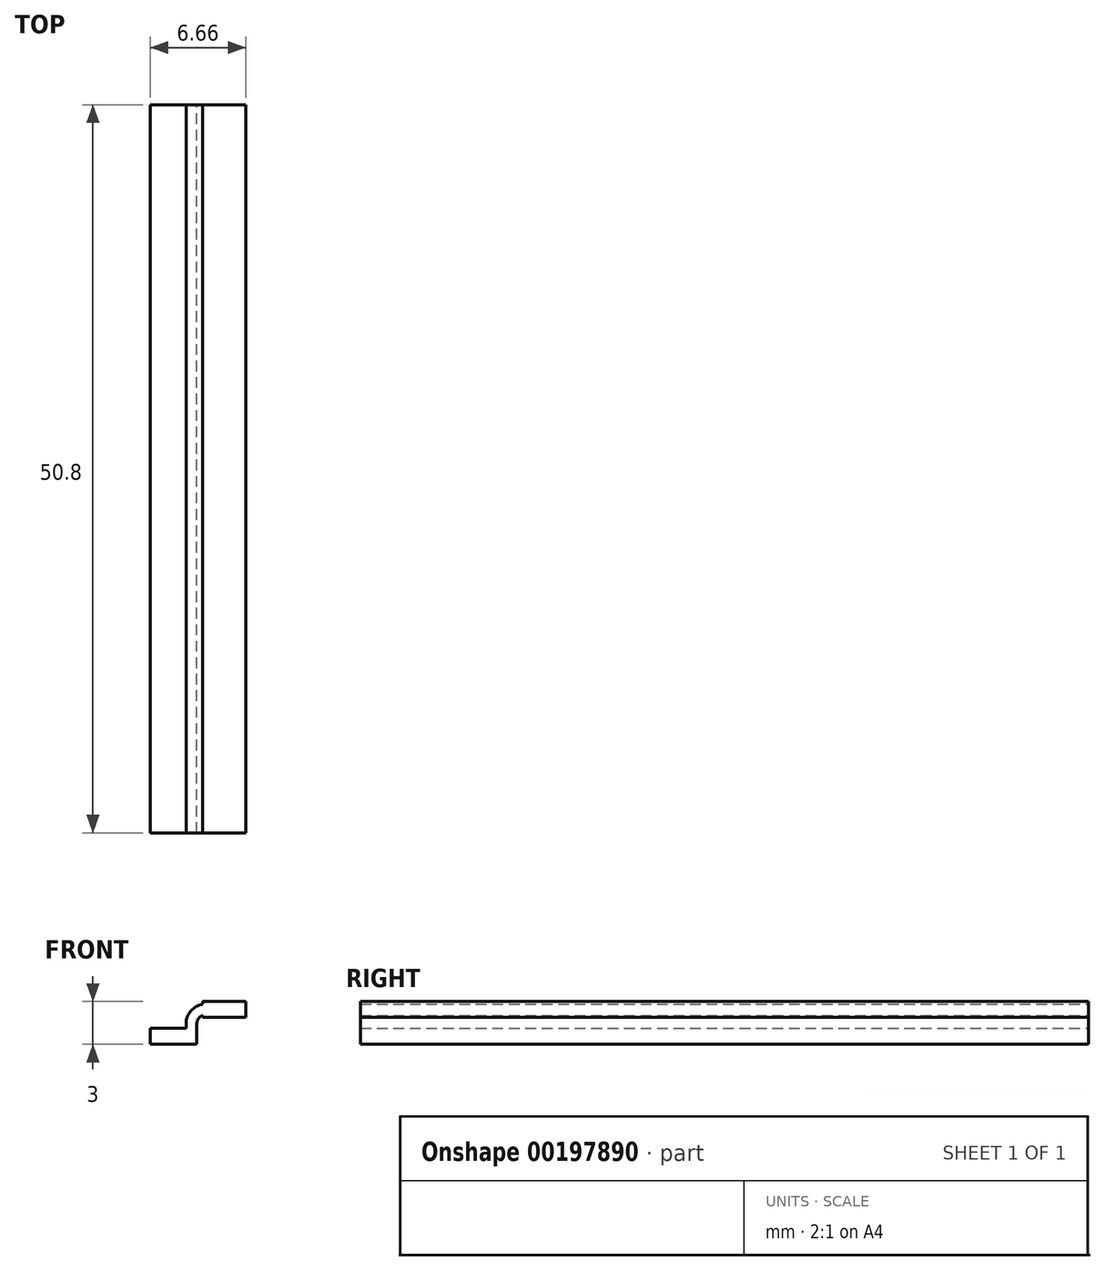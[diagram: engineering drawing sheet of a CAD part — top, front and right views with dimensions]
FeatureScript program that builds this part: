
annotation { "Feature Type Name" : "Feature", "Feature Type Description" : "" }
export const myFeature = defineFeature(function(context is Context, id is Id, definition is map)
    precondition{}
    {
        {
            var Q0;
            Q0=qCreatedBy(makeId("Front.planeOp"),FACE);
            var sketch = newSketch(context, id + "F0", { "sketchPlane" : qUnion([Q0])});
            skLineSegment(sketch, "E0.bottom", {"start": v(1.63, -0.56) * mm, "end": v(-1.63, -0.56) * mm});
            skLineSegment(sketch, "E0.top", {"start": v(1.62, 0.56) * mm, "end": v(-1.63, 0.56) * mm});
            skLineSegment(sketch, "E0.left", {"start": v(1.63, -0.56) * mm, "end": v(1.63, 0.56) * mm});
            skLineSegment(sketch, "E0.right", {"start": v(-1.63, -0.56) * mm, "end": v(-1.63, 0.56) * mm});
            skPoint(sketch, "E0.middle", {"position": v(0, 0) * mm});
            skLineSegment(sketch, "E1.bottom", {"start": v(2.04, 1.31) * mm, "end": v(5.04, 1.31) * mm});
            skLineSegment(sketch, "E1.top", {"start": v(2.04, 2.44) * mm, "end": v(5.04, 2.44) * mm});
            skLineSegment(sketch, "E1.left", {"start": v(2.04, 1.31) * mm, "end": v(2.04, 2.44) * mm});
            skLineSegment(sketch, "E1.right", {"start": v(5.04, 1.31) * mm, "end": v(5.04, 2.44) * mm});
            skPoint(sketch, "E1.middle", {"position": v(3.54, 1.88) * mm});
            skLineSegment(sketch, "E2", {"start": v(1.62, 0.56) * mm, "end": v(1.62, 0.88) * mm});
            skArc(sketch, "E3", {"start": v(1.62, 0.88) * mm, "mid": v(1.8, 1.32) * mm, "end": v(2.25, 1.5) * mm});
            skLineSegment(sketch, "E4", {"start": v(2.25, 1.5) * mm, "end": v(3.38, 1.5) * mm});
            skLineSegment(sketch, "E5.0", {"start": v(2.25, 2.25) * mm, "end": v(3.38, 2.25) * mm});
            skArc(sketch, "E5.1", {"start": v(0.87, 0.88) * mm, "mid": v(1.28, 1.85) * mm, "end": v(2.25, 2.25) * mm});
            skLineSegment(sketch, "E5.2", {"start": v(0.87, 0.56) * mm, "end": v(0.87, 0.88) * mm});
            skLineSegment(sketch, "E6", {"start": v(3.38, 1.5) * mm, "end": v(3.38, 2.25) * mm});
            skFitSpline(sketch, "E7", {"points": [v(-1.63, 0.56) * mm, v(2.04, 2.23) * mm], "startDerivative": vector(-0.1, 2.67) * mm, "endDerivative": vector(6.12, -0.1) * mm});
            skSolve(sketch);
        }
        {
            var Q0;
            Q0=makeQuery(id+"F0.imprint","IMPRINT",FACE,{"disambiguationData":[TD([[makeQuery(id+"F0.imprint","IMPRINT",EDGE,{"derivedFrom":sQuery(id+"F0.wireOp",EDGE,"E0.bottom")}),-1.0]])]});
            var Q1;
            {var subQ1=sQuery(id+"F0.wireOp",EDGE,"E2");Q1=makeQuery(id+"F0.imprint","IMPRINT",FACE,{"disambiguationData":[TD([[makeQuery(id+"F0.imprint","IMPRINT",EDGE,{"derivedFrom":subQ1}),1.0]])]});}
            var Q2;
            {var subQ1=sQuery(id+"F0.wireOp",EDGE,"E4");Q2=makeQuery(id+"F0.imprint","IMPRINT",FACE,{"disambiguationData":[TD([[makeQuery(id+"F0.imprint","IMPRINT",EDGE,{"derivedFrom":subQ1}),1.0]])]});}
            var Q3;
            {var subQ4=sQuery(id+"F0.wireOp",EDGE,"E1.bottom");Q3=makeQuery(id+"F0.imprint","IMPRINT",FACE,{"disambiguationData":[TD([[makeQuery(id+"F0.imprint","IMPRINT",EDGE,{"derivedFrom":subQ4}),1.0]])]});}
            extrude(context, id + "F1", {"entities" : qUnion([Q0, Q1, Q2, Q3]), "endBound" : BoundingType.SYMMETRIC, "depth" : 50.8 * mm});
        }
    });
